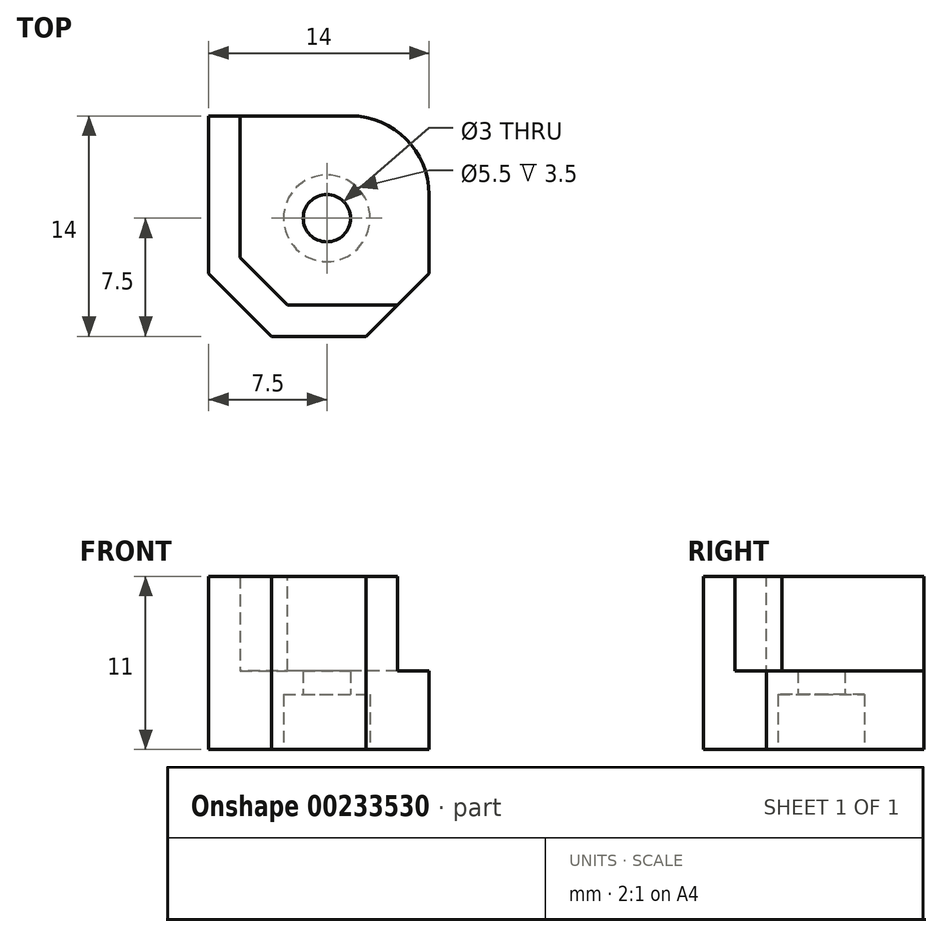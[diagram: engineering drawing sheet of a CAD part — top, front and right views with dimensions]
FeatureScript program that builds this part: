
annotation { "Feature Type Name" : "Feature", "Feature Type Description" : "" }
export const myFeature = defineFeature(function(context is Context, id is Id, definition is map)
    precondition{}
    {
        {
            var Q0;
            Q0=qCreatedBy(makeId("Top.planeOp"),FACE);
            var sketch = newSketch(context, id + "F0", { "sketchPlane" : qUnion([Q0])});
            skLineSegment(sketch, "E0.bottom", {"start": v(6, -6) * mm, "end": v(-6, -6) * mm});
            skLineSegment(sketch, "E0.top", {"start": v(6, 6) * mm, "end": v(-6, 6) * mm});
            skLineSegment(sketch, "E0.left", {"start": v(6, -6) * mm, "end": v(6, 6) * mm});
            skLineSegment(sketch, "E0.right", {"start": v(-6, -6) * mm, "end": v(-6, 6) * mm});
            skPoint(sketch, "E0.middle", {"position": v(0, 0) * mm});
            skCircle(sketch, "E1", {"center": v(-0.5, -0.5) * mm, "radius": 1.5 * mm});
            skLineSegment(sketch, "E2.top", {"start": v(6, -8) * mm, "end": v(-6, -8) * mm});
            skLineSegment(sketch, "E2.left", {"start": v(6, -6) * mm, "end": v(6, -8) * mm});
            skLineSegment(sketch, "E2.right", {"start": v(-6, -6) * mm, "end": v(-6, -8) * mm});
            skLineSegment(sketch, "E3.bottom", {"start": v(-6, 6) * mm, "end": v(-8, 6) * mm});
            skLineSegment(sketch, "E3.top", {"start": v(-6, -8) * mm, "end": v(-8, -8) * mm});
            skLineSegment(sketch, "E3.left", {"start": v(-6, 6) * mm, "end": v(-6, -8) * mm});
            skLineSegment(sketch, "E3.right", {"start": v(-8, 6) * mm, "end": v(-8, -8) * mm});
            skSolve(sketch);
        }
        {
            var Q0;
            Q0=makeQuery(id+"F0.imprint","IMPRINT",FACE,{"disambiguationData":[TD([[makeQuery(id+"F0.imprint","IMPRINT",EDGE,{"derivedFrom":sQuery(id+"F0.wireOp",EDGE,"E0.bottom")}),-1.0]])]});
            var Q1;
            {var subQ2=sQuery(id+"F0.wireOp",EDGE,"E0.top");Q1=makeQuery(id+"F0.imprint","IMPRINT",FACE,{"disambiguationData":[TD([[makeQuery(id+"F0.imprint","IMPRINT",EDGE,{"derivedFrom":subQ2}),1.0]])]});}
            var Q2;
            {var subQ0=sQuery(id+"F0.wireOp",EDGE,"E0.bottom");Q2=makeQuery(id+"F0.imprint","IMPRINT",FACE,{"disambiguationData":[TD([[makeQuery(id+"F0.imprint","IMPRINT",EDGE,{"derivedFrom":subQ0}),1.0]])]});}
            var Q3;
            {var subQ3=sQuery(id+"F0.wireOp",EDGE,"E3.bottom");Q3=makeQuery(id+"F0.imprint","IMPRINT",FACE,{"disambiguationData":[TD([[makeQuery(id+"F0.imprint","IMPRINT",EDGE,{"derivedFrom":subQ3}),1.0]])]});}
            extrude(context, id + "F1", {"entities" : qUnion([Q0, Q1, Q2, Q3]), "depth" : 5 * mm});
        }
        {
            var Q0;
            Q0=makeQuery(id+"F1.opExtrude","CAP_FACE",FACE,{"disambiguationData":[OSD([sQuery(id+"F0.wireOp",EDGE,"E0.top"),sQuery(id+"F0.wireOp",EDGE,"E0.left"),sQuery(id+"F0.wireOp",EDGE,"E1"),sQuery(id+"F0.wireOp",EDGE,"E2.top"),sQuery(id+"F0.wireOp",EDGE,"E2.left"),sQuery(id+"F0.wireOp",EDGE,"E3.bottom"),sQuery(id+"F0.wireOp",EDGE,"E3.top"),sQuery(id+"F0.wireOp",EDGE,"E3.right")])],"isStart":false});
            var sketch = newSketch(context, id + "F2", { "sketchPlane" : qUnion([Q0])});
            skLineSegment(sketch, "E4.bottom", {"start": v(-8, 6) * mm, "end": v(-6, 6) * mm});
            skLineSegment(sketch, "E4.top", {"start": v(-8, -8) * mm, "end": v(-6, -8) * mm});
            skLineSegment(sketch, "E4.left", {"start": v(-8, 6) * mm, "end": v(-8, -8) * mm});
            skLineSegment(sketch, "E4.right", {"start": v(-6, 6) * mm, "end": v(-6, -8) * mm});
            skLineSegment(sketch, "E5.bottom", {"start": v(6, -8) * mm, "end": v(-8, -8) * mm});
            skLineSegment(sketch, "E5.top", {"start": v(6, -6) * mm, "end": v(-8, -6) * mm});
            skLineSegment(sketch, "E5.left", {"start": v(6, -8) * mm, "end": v(6, -6) * mm});
            skLineSegment(sketch, "E5.right", {"start": v(-8, -8) * mm, "end": v(-8, -6) * mm});
            skSolve(sketch);
        }
        {
            var Q0;
            {var subQ9=sQuery(id+"F2.wireOp",EDGE,"E4.bottom");Q0=makeQuery(id+"F2.imprint","IMPRINT",FACE,{"disambiguationData":[TD([[makeQuery(id+"F2.imprint","IMPRINT",EDGE,{"derivedFrom":subQ9}),1.0]])]});}
            var Q1;
            {var subQ0=sQuery(id+"F2.wireOp",EDGE,"E5.left");Q1=makeQuery(id+"F2.imprint","IMPRINT",FACE,{"disambiguationData":[TD([[makeQuery(id+"F2.imprint","IMPRINT",EDGE,{"derivedFrom":subQ0}),1.0]])]});}
            var Q2;
            {var subQ0=sQuery(id+"F2.wireOp",EDGE,"E5.top");var subQ1=sQuery(id+"F2.wireOp",EDGE,"E4.right");var subQ2=makeQuery(id+"F2.imprint","INTERSECT",VERTEX,{"derivedFrom":[subQ1,subQ0]});Q2=makeQuery(id+"F2.imprint","IMPRINT",FACE,{"disambiguationData":[TD([[makeQuery(id+"F2.imprint","IMPRINT",EDGE,{"disambiguationData":[TD([[subQ2,-1.0]])],"derivedFrom":subQ1}),-1.0]])]});}
            extrude(context, id + "F3", {"entities" : qUnion([Q0, Q1, Q2]), "operationType" : NewBodyOperationType.ADD, "depth" : 6 * mm});
        }
        {
            var Q0;
            Q0=makeQuery(id+"F1.opExtrude","CAP_FACE",FACE,{"disambiguationData":[OSD([sQuery(id+"F0.wireOp",EDGE,"E0.top"),sQuery(id+"F0.wireOp",EDGE,"E0.left"),sQuery(id+"F0.wireOp",EDGE,"E1"),sQuery(id+"F0.wireOp",EDGE,"E2.top"),sQuery(id+"F0.wireOp",EDGE,"E2.left"),sQuery(id+"F0.wireOp",EDGE,"E3.bottom"),sQuery(id+"F0.wireOp",EDGE,"E3.top"),sQuery(id+"F0.wireOp",EDGE,"E3.right")])],"isStart":true});
            var sketch = newSketch(context, id + "F4", { "sketchPlane" : qUnion([Q0])});
            skCircle(sketch, "E6", {"center": v(-0.5, 0.5) * mm, "radius": 2.75 * mm});
            skSolve(sketch);
        }
        {
            var Q0;
            Q0 = qSketchRegion(id + "F4", true);
            extrude(context, id + "F5", {"entities" : qUnion([Q0]), "operationType" : NewBodyOperationType.REMOVE, "oppositeDirection" : true, "depth" : 3.5 * mm});
        }
        {
            var Q0;
            Q0=makeQuery(id+"F3.opExtrude","SWEPT_EDGE",EDGE,{"disambiguationData":[OSD([sQuery(id+"F2.wireOp",EDGE,"E4.right"),sQuery(id+"F2.wireOp",EDGE,"E5.top")])]});
            chamfer(context, id + "F6", {"entities" : qUnion([Q0]), "width" : 3 * mm, "tangentPropagation" : true});
        }
        {
            var Q0;
            Q0=makeQuery(id+"F3.boolean.opBoolean","MERGE",EDGE,{"derivedFrom":[makeQuery(id+"F1.opExtrude","SWEPT_EDGE",EDGE,{"disambiguationData":[OSD([sQuery(id+"F0.wireOp",EDGE,"E3.top"),sQuery(id+"F0.wireOp",EDGE,"E3.right")])]}),makeQuery(id+"F3.opExtrude","SWEPT_EDGE",EDGE,{"disambiguationData":[OSD([sQuery(id+"F2.wireOp",EDGE,"E5.bottom"),sQuery(id+"F2.wireOp",EDGE,"E5.right")])]})]});
            chamfer(context, id + "F7", {"entities" : qUnion([Q0]), "width" : 4 * mm, "tangentPropagation" : true});
        }
        {
            var Q0;
            Q0=makeQuery(id+"F1.opExtrude","SWEPT_EDGE",EDGE,{"disambiguationData":[OSD([sQuery(id+"F0.wireOp",EDGE,"E0.top"),sQuery(id+"F0.wireOp",EDGE,"E0.left")])]});
            fillet(context, id + "F8", {"entities" : qUnion([Q0]), "radius" : 5 * mm, "tangentPropagation" : true, "allowEdgeOverflow" : false});
        }
    });
